annotation { "Feature Type Name" : "Feature", "Feature Type Description" : "" }
export const myFeature = defineFeature(function(context is Context, id is Id, definition is map)
    precondition{}
    {
        {
            var Q0;
            Q0=qCreatedBy(makeId("Front.planeOp"),FACE);
            var sketch = newSketch(context, id + "F0", { "sketchPlane" : qUnion([Q0])});
            skCircle(sketch, "E0", {"center": v(0, 0) * mm, "radius": 10.5 * mm});
            skCircle(sketch, "E1", {"center": v(0, 0) * mm, "radius": 13 * mm});
            skArc(sketch, "E2", {"start": v(11.57, 14.44) * mm, "mid": v(9.32, 12.76) * mm, "end": v(7.8, 10.4) * mm});
            skArc(sketch, "E3.MirrorCS", {"start": v(-11.57, 14.44) * mm, "mid": v(-9.32, 12.76) * mm, "end": v(-7.8, 10.4) * mm});
            skLineSegment(sketch, "E4", {"start": v(11.57, 14.44) * mm, "end": v(-11.57, 14.44) * mm});
            skSolve(sketch);
        }
        {
            var Q0;
            Q0=makeQuery(id+"F0.imprint","IMPRINT",FACE,{"disambiguationData":[TD([[makeQuery(id+"F0.imprint","IMPRINT",EDGE,{"derivedFrom":sQuery(id+"F0.wireOp",EDGE,"E0")}),-1.0]])]});
            extrude(context, id + "F1", {"entities" : qUnion([Q0]), "depth" : 8 * mm, "offsetDistance" : 25 * mm});
        }
        {
            var Q0;
            Q0=makeQuery(id+"F1.opExtrude","CAP_EDGE",EDGE,{"disambiguationData":[OSD([sQuery(id+"F0.wireOp",EDGE,"E1")])],"isStart":true});
            var Q1;
            Q1=makeQuery(id+"F1.opExtrude","CAP_EDGE",EDGE,{"disambiguationData":[OSD([sQuery(id+"F0.wireOp",EDGE,"E1")])],"isStart":false});
            var Q2;
            Q2=makeQuery(id+"F1.opExtrude","CAP_EDGE",EDGE,{"disambiguationData":[OSD([sQuery(id+"F0.wireOp",EDGE,"E0")])],"isStart":false});
            var Q3;
            Q3=makeQuery(id+"F1.opExtrude","CAP_EDGE",EDGE,{"disambiguationData":[OSD([sQuery(id+"F0.wireOp",EDGE,"E0")])],"isStart":true});
            fillet(context, id + "F2", {"entities" : qUnion([Q0, Q1, Q2, Q3]), "radius" : 1 * mm, "tangentPropagation" : true, "allowEdgeOverflow" : false});
        }
        {
            var Q0;
            {var subQ0=sQuery(id+"F0.wireOp",EDGE,"E2");Q0=makeQuery(id+"F0.imprint","IMPRINT",FACE,{"disambiguationData":[TD([[makeQuery(id+"F0.imprint","IMPRINT",EDGE,{"derivedFrom":subQ0}),-1.0]])]});}
            extrude(context, id + "F3", {"entities" : qUnion([Q0]), "operationType" : NewBodyOperationType.ADD, "depth" : 8 * mm, "offsetDistance" : 25 * mm});
        }
        {
            var Q0;
            Q0=makeQuery(id+"F3.opExtrude","SWEPT_FACE",FACE,{"disambiguationData":[OSD([sQuery(id+"F0.wireOp",EDGE,"E4")])]});
            var sketch = newSketch(context, id + "F4", { "sketchPlane" : qUnion([Q0])});
            skCircle(sketch, "E5.cCircle", {"center": v(10.18, -4.7) * mm, "radius": 1 * mm, "construction": true});
            skLineSegment(sketch, "E5.0", {"start": v(9.34, -5.4) * mm, "end": v(9.1, -4.48) * mm});
            skLineSegment(sketch, "E5.1", {"start": v(9.1, -4.48) * mm, "end": v(9.68, -3.72) * mm});
            skLineSegment(sketch, "E5.2", {"start": v(9.68, -3.72) * mm, "end": v(10.64, -3.7) * mm});
            skLineSegment(sketch, "E5.3", {"start": v(10.64, -3.7) * mm, "end": v(11.25, -4.43) * mm});
            skLineSegment(sketch, "E5.4", {"start": v(11.25, -4.43) * mm, "end": v(11.06, -5.37) * mm});
            skLineSegment(sketch, "E5.5", {"start": v(11.06, -5.37) * mm, "end": v(10.2, -5.8) * mm});
            skLineSegment(sketch, "E5.6", {"start": v(10.2, -5.8) * mm, "end": v(9.34, -5.4) * mm});
            skPoint(sketch, "E5.0.midPoint", {"position": v(9.22, -4.94) * mm});
            skCircle(sketch, "E6", {"center": v(10.18, -4.7) * mm, "radius": 1 * mm});
            skText(sketch, "E7", { "text": "Natsu Lee", "fontName": "NotoSansCJKjp-Regular.otf"});
            skLineSegment(sketch, "E8", {"start": v(9.68, -3.72) * mm, "end": v(10.2, -5.8) * mm});
            skLineSegment(sketch, "E9", {"start": v(10.64, -3.7) * mm, "end": v(10.2, -5.8) * mm});
            skCircle(sketch, "E10", {"center": v(-9.7, -1.1) * mm, "radius": 0.75 * mm});
            skArc(sketch, "E11", {"start": v(-9.78, -0.68) * mm, "mid": v(-10, -0.61) * mm, "end": v(-10.16, -0.8) * mm});
            skCircle(sketch, "E12", {"center": v(-9.95, -0.81) * mm, "radius": 0.11 * mm});
            skArc(sketch, "E13", {"start": v(-10.03, -1.41) * mm, "mid": v(-9.63, -1.7) * mm, "end": v(-9.23, -1.41) * mm});
            skArc(sketch, "E14.0", {"start": v(-9.73, -0.64) * mm, "mid": v(-10.03, -0.55) * mm, "end": v(-10.23, -0.8) * mm});
            skLineSegment(sketch, "E15", {"start": v(-10.23, -0.8) * mm, "end": v(-10.16, -0.8) * mm});
            skLineSegment(sketch, "E16", {"start": v(-9.78, -0.68) * mm, "end": v(-9.73, -0.64) * mm});
            skLineSegment(sketch, "E17", {"start": v(-9.63, -0.62) * mm, "end": v(-9.7, -1.1) * mm, "construction": true});
            skCircle(sketch, "E18.MirrorC", {"center": v(-9.38, -0.9) * mm, "radius": 0.11 * mm});
            skArc(sketch, "E19.MirrorCS", {"start": v(-9.5, -0.73) * mm, "mid": v(-9.26, -0.73) * mm, "end": v(-9.18, -0.95) * mm});
            skLineSegment(sketch, "E20.MirrorCS", {"start": v(-9.1, -0.96) * mm, "end": v(-9.18, -0.95) * mm});
            skArc(sketch, "E21.MirrorCS", {"start": v(-9.54, -0.67) * mm, "mid": v(-9.22, -0.67) * mm, "end": v(-9.1, -0.96) * mm});
            skLineSegment(sketch, "E22.MirrorCS", {"start": v(-9.5, -0.73) * mm, "end": v(-9.54, -0.67) * mm});
            skCircle(sketch, "E23", {"center": v(-9.7, -1.1) * mm, "radius": 0.05 * mm});
            skArc(sketch, "E24.0", {"start": v(-10, -1.4) * mm, "mid": v(-9.63, -1.68) * mm, "end": v(-9.25, -1.4) * mm});
            skLineSegment(sketch, "E25", {"start": v(-10.03, -1.41) * mm, "end": v(-10, -1.4) * mm});
            skLineSegment(sketch, "E26", {"start": v(-9.25, -1.4) * mm, "end": v(-9.23, -1.41) * mm});
            skArc(sketch, "E27.1.0.0", {"start": v(-6, -1.4) * mm, "mid": v(-5.63, -1.68) * mm, "end": v(-5.25, -1.4) * mm});
            skArc(sketch, "E27.1.0.1", {"start": v(-6.03, -1.41) * mm, "mid": v(-5.63, -1.7) * mm, "end": v(-5.23, -1.41) * mm});
            skLineSegment(sketch, "E27.1.0.2", {"start": v(-6.03, -1.41) * mm, "end": v(-6, -1.4) * mm});
            skLineSegment(sketch, "E27.1.0.3", {"start": v(-5.25, -1.4) * mm, "end": v(-5.23, -1.41) * mm});
            skCircle(sketch, "E27.1.0.4", {"center": v(-5.7, -1.1) * mm, "radius": 0.05 * mm});
            skCircle(sketch, "E27.1.0.5", {"center": v(-5.95, -0.81) * mm, "radius": 0.11 * mm});
            skArc(sketch, "E27.1.0.6", {"start": v(-5.78, -0.68) * mm, "mid": v(-6, -0.61) * mm, "end": v(-6.16, -0.8) * mm});
            skLineSegment(sketch, "E27.1.0.7", {"start": v(-6.23, -0.8) * mm, "end": v(-6.16, -0.8) * mm});
            skArc(sketch, "E27.1.0.8", {"start": v(-5.73, -0.64) * mm, "mid": v(-6.03, -0.55) * mm, "end": v(-6.23, -0.8) * mm});
            skLineSegment(sketch, "E27.1.0.9", {"start": v(-5.78, -0.68) * mm, "end": v(-5.73, -0.64) * mm});
            skLineSegment(sketch, "E27.1.0.10", {"start": v(-5.5, -0.73) * mm, "end": v(-5.54, -0.67) * mm});
            skArc(sketch, "E27.1.0.11", {"start": v(-5.54, -0.67) * mm, "mid": v(-5.22, -0.67) * mm, "end": v(-5.1, -0.96) * mm});
            skArc(sketch, "E27.1.0.12", {"start": v(-5.5, -0.73) * mm, "mid": v(-5.26, -0.73) * mm, "end": v(-5.18, -0.95) * mm});
            skCircle(sketch, "E27.1.0.13", {"center": v(-5.38, -0.9) * mm, "radius": 0.11 * mm});
            skLineSegment(sketch, "E27.1.0.14", {"start": v(-5.1, -0.96) * mm, "end": v(-5.18, -0.95) * mm});
            skArc(sketch, "E27.2.0.0", {"start": v(-2, -1.4) * mm, "mid": v(-1.63, -1.68) * mm, "end": v(-1.25, -1.4) * mm});
            skArc(sketch, "E27.2.0.1", {"start": v(-2.03, -1.41) * mm, "mid": v(-1.63, -1.7) * mm, "end": v(-1.23, -1.41) * mm});
            skLineSegment(sketch, "E27.2.0.2", {"start": v(-2.03, -1.41) * mm, "end": v(-2, -1.4) * mm});
            skLineSegment(sketch, "E27.2.0.3", {"start": v(-1.25, -1.4) * mm, "end": v(-1.23, -1.41) * mm});
            skCircle(sketch, "E27.2.0.4", {"center": v(-1.7, -1.1) * mm, "radius": 0.05 * mm});
            skCircle(sketch, "E27.2.0.5", {"center": v(-1.95, -0.81) * mm, "radius": 0.11 * mm});
            skArc(sketch, "E27.2.0.6", {"start": v(-1.78, -0.68) * mm, "mid": v(-2, -0.61) * mm, "end": v(-2.16, -0.8) * mm});
            skLineSegment(sketch, "E27.2.0.7", {"start": v(-2.23, -0.8) * mm, "end": v(-2.16, -0.8) * mm});
            skArc(sketch, "E27.2.0.8", {"start": v(-1.73, -0.64) * mm, "mid": v(-2.03, -0.55) * mm, "end": v(-2.23, -0.8) * mm});
            skLineSegment(sketch, "E27.2.0.9", {"start": v(-1.78, -0.68) * mm, "end": v(-1.73, -0.64) * mm});
            skLineSegment(sketch, "E27.2.0.10", {"start": v(-1.5, -0.73) * mm, "end": v(-1.54, -0.67) * mm});
            skArc(sketch, "E27.2.0.11", {"start": v(-1.54, -0.67) * mm, "mid": v(-1.22, -0.67) * mm, "end": v(-1.1, -0.96) * mm});
            skArc(sketch, "E27.2.0.12", {"start": v(-1.5, -0.73) * mm, "mid": v(-1.26, -0.73) * mm, "end": v(-1.18, -0.95) * mm});
            skCircle(sketch, "E27.2.0.13", {"center": v(-1.38, -0.9) * mm, "radius": 0.11 * mm});
            skLineSegment(sketch, "E27.2.0.14", {"start": v(-1.1, -0.96) * mm, "end": v(-1.18, -0.95) * mm});
            skArc(sketch, "E27.3.0.0", {"start": v(2, -1.4) * mm, "mid": v(2.37, -1.68) * mm, "end": v(2.75, -1.4) * mm});
            skArc(sketch, "E27.3.0.1", {"start": v(1.97, -1.41) * mm, "mid": v(2.37, -1.7) * mm, "end": v(2.77, -1.41) * mm});
            skLineSegment(sketch, "E27.3.0.2", {"start": v(1.97, -1.41) * mm, "end": v(2, -1.4) * mm});
            skLineSegment(sketch, "E27.3.0.3", {"start": v(2.75, -1.4) * mm, "end": v(2.77, -1.41) * mm});
            skCircle(sketch, "E27.3.0.4", {"center": v(2.3, -1.1) * mm, "radius": 0.05 * mm});
            skCircle(sketch, "E27.3.0.5", {"center": v(2.05, -0.81) * mm, "radius": 0.11 * mm});
            skArc(sketch, "E27.3.0.6", {"start": v(2.22, -0.68) * mm, "mid": v(2, -0.61) * mm, "end": v(1.84, -0.8) * mm});
            skLineSegment(sketch, "E27.3.0.7", {"start": v(1.77, -0.8) * mm, "end": v(1.84, -0.8) * mm});
            skArc(sketch, "E27.3.0.8", {"start": v(2.27, -0.64) * mm, "mid": v(1.97, -0.55) * mm, "end": v(1.77, -0.8) * mm});
            skLineSegment(sketch, "E27.3.0.9", {"start": v(2.22, -0.68) * mm, "end": v(2.27, -0.64) * mm});
            skLineSegment(sketch, "E27.3.0.10", {"start": v(2.5, -0.73) * mm, "end": v(2.46, -0.67) * mm});
            skArc(sketch, "E27.3.0.11", {"start": v(2.46, -0.67) * mm, "mid": v(2.78, -0.67) * mm, "end": v(2.9, -0.96) * mm});
            skArc(sketch, "E27.3.0.12", {"start": v(2.5, -0.73) * mm, "mid": v(2.74, -0.73) * mm, "end": v(2.82, -0.95) * mm});
            skCircle(sketch, "E27.3.0.13", {"center": v(2.62, -0.9) * mm, "radius": 0.11 * mm});
            skLineSegment(sketch, "E27.3.0.14", {"start": v(2.9, -0.96) * mm, "end": v(2.82, -0.95) * mm});
            skArc(sketch, "E27.4.0.0", {"start": v(6, -1.4) * mm, "mid": v(6.37, -1.68) * mm, "end": v(6.75, -1.4) * mm});
            skArc(sketch, "E27.4.0.1", {"start": v(5.97, -1.41) * mm, "mid": v(6.37, -1.7) * mm, "end": v(6.77, -1.41) * mm});
            skLineSegment(sketch, "E27.4.0.2", {"start": v(5.97, -1.41) * mm, "end": v(6, -1.4) * mm});
            skLineSegment(sketch, "E27.4.0.3", {"start": v(6.75, -1.4) * mm, "end": v(6.77, -1.41) * mm});
            skCircle(sketch, "E27.4.0.4", {"center": v(6.3, -1.1) * mm, "radius": 0.05 * mm});
            skCircle(sketch, "E27.4.0.5", {"center": v(6.05, -0.81) * mm, "radius": 0.11 * mm});
            skArc(sketch, "E27.4.0.6", {"start": v(6.22, -0.68) * mm, "mid": v(6, -0.61) * mm, "end": v(5.84, -0.8) * mm});
            skLineSegment(sketch, "E27.4.0.7", {"start": v(5.77, -0.8) * mm, "end": v(5.84, -0.8) * mm});
            skArc(sketch, "E27.4.0.8", {"start": v(6.27, -0.64) * mm, "mid": v(5.97, -0.55) * mm, "end": v(5.77, -0.8) * mm});
            skLineSegment(sketch, "E27.4.0.9", {"start": v(6.22, -0.68) * mm, "end": v(6.27, -0.64) * mm});
            skLineSegment(sketch, "E27.4.0.10", {"start": v(6.5, -0.73) * mm, "end": v(6.46, -0.67) * mm});
            skArc(sketch, "E27.4.0.11", {"start": v(6.46, -0.67) * mm, "mid": v(6.78, -0.67) * mm, "end": v(6.9, -0.96) * mm});
            skArc(sketch, "E27.4.0.12", {"start": v(6.5, -0.73) * mm, "mid": v(6.74, -0.73) * mm, "end": v(6.82, -0.95) * mm});
            skCircle(sketch, "E27.4.0.13", {"center": v(6.62, -0.9) * mm, "radius": 0.11 * mm});
            skLineSegment(sketch, "E27.4.0.14", {"start": v(6.9, -0.96) * mm, "end": v(6.82, -0.95) * mm});
            skArc(sketch, "E27.5.0.0", {"start": v(10, -1.4) * mm, "mid": v(10.37, -1.68) * mm, "end": v(10.75, -1.4) * mm});
            skArc(sketch, "E27.5.0.1", {"start": v(9.97, -1.41) * mm, "mid": v(10.37, -1.7) * mm, "end": v(10.77, -1.41) * mm});
            skLineSegment(sketch, "E27.5.0.2", {"start": v(9.97, -1.41) * mm, "end": v(10, -1.4) * mm});
            skLineSegment(sketch, "E27.5.0.3", {"start": v(10.75, -1.4) * mm, "end": v(10.77, -1.41) * mm});
            skCircle(sketch, "E27.5.0.4", {"center": v(10.3, -1.1) * mm, "radius": 0.05 * mm});
            skCircle(sketch, "E27.5.0.5", {"center": v(10.05, -0.81) * mm, "radius": 0.11 * mm});
            skArc(sketch, "E27.5.0.6", {"start": v(10.22, -0.68) * mm, "mid": v(10, -0.61) * mm, "end": v(9.84, -0.8) * mm});
            skLineSegment(sketch, "E27.5.0.7", {"start": v(9.77, -0.8) * mm, "end": v(9.84, -0.8) * mm});
            skArc(sketch, "E27.5.0.8", {"start": v(10.27, -0.64) * mm, "mid": v(9.97, -0.55) * mm, "end": v(9.77, -0.8) * mm});
            skLineSegment(sketch, "E27.5.0.9", {"start": v(10.22, -0.68) * mm, "end": v(10.27, -0.64) * mm});
            skLineSegment(sketch, "E27.5.0.10", {"start": v(10.5, -0.73) * mm, "end": v(10.46, -0.67) * mm});
            skArc(sketch, "E27.5.0.11", {"start": v(10.46, -0.67) * mm, "mid": v(10.78, -0.67) * mm, "end": v(10.9, -0.96) * mm});
            skArc(sketch, "E27.5.0.12", {"start": v(10.5, -0.73) * mm, "mid": v(10.74, -0.73) * mm, "end": v(10.82, -0.95) * mm});
            skCircle(sketch, "E27.5.0.13", {"center": v(10.62, -0.9) * mm, "radius": 0.11 * mm});
            skLineSegment(sketch, "E27.5.0.14", {"start": v(10.9, -0.96) * mm, "end": v(10.82, -0.95) * mm});
            skLineSegment(sketch, "E27.direction1", {"start": v(-10, -1.4) * mm, "end": v(-6, -1.4) * mm, "construction": true});
            const initialGuessF4  = {"E7": [-0.01103, -0.00537, 1, 0, 0.00311]};
            skSetInitialGuess(sketch, initialGuessF4);
            skSolve(sketch);
        }
        {
            var Q0;
            {var subQ0=sQuery(id+"F4.wireOp",EDGE,"E5.5");var subQ1=sQuery(id+"F4.wireOp",EDGE,"E5.4");var subQ2=makeQuery(id+"F4.imprint","INTERSECT",VERTEX,{"derivedFrom":[subQ1,subQ0]});Q0=makeQuery(id+"F4.imprint","IMPRINT",FACE,{"disambiguationData":[TD([[makeQuery(id+"F4.imprint","IMPRINT",EDGE,{"disambiguationData":[TD([[subQ2,1.0]])],"derivedFrom":subQ1}),-1.0]])]});}
            var Q1;
            {var subQ0=sQuery(id+"F4.wireOp",EDGE,"E5.4");var subQ1=sQuery(id+"F4.wireOp",EDGE,"E5.3");var subQ2=makeQuery(id+"F4.imprint","INTERSECT",VERTEX,{"derivedFrom":[subQ1,subQ0]});Q1=makeQuery(id+"F4.imprint","IMPRINT",FACE,{"disambiguationData":[TD([[makeQuery(id+"F4.imprint","IMPRINT",EDGE,{"disambiguationData":[TD([[subQ2,1.0]])],"derivedFrom":subQ1}),-1.0]])]});}
            var Q2;
            {var subQ0=sQuery(id+"F4.wireOp",EDGE,"E5.3");var subQ1=sQuery(id+"F4.wireOp",EDGE,"E5.2");var subQ2=makeQuery(id+"F4.imprint","INTERSECT",VERTEX,{"derivedFrom":[subQ1,subQ0]});Q2=makeQuery(id+"F4.imprint","IMPRINT",FACE,{"disambiguationData":[TD([[makeQuery(id+"F4.imprint","IMPRINT",EDGE,{"disambiguationData":[TD([[subQ2,1.0]])],"derivedFrom":subQ1}),-1.0]])]});}
            var Q3;
            {var subQ0=sQuery(id+"F4.wireOp",EDGE,"E5.2");var subQ1=sQuery(id+"F4.wireOp",EDGE,"E5.1");var subQ2=makeQuery(id+"F4.imprint","INTERSECT",VERTEX,{"derivedFrom":[subQ1,subQ0]});Q3=makeQuery(id+"F4.imprint","IMPRINT",FACE,{"disambiguationData":[TD([[makeQuery(id+"F4.imprint","IMPRINT",EDGE,{"disambiguationData":[TD([[subQ2,1.0]])],"derivedFrom":subQ1}),-1.0]])]});}
            var Q4;
            {var subQ0=sQuery(id+"F4.wireOp",EDGE,"E5.1");var subQ1=sQuery(id+"F4.wireOp",EDGE,"E5.0");var subQ2=makeQuery(id+"F4.imprint","INTERSECT",VERTEX,{"derivedFrom":[subQ1,subQ0]});Q4=makeQuery(id+"F4.imprint","IMPRINT",FACE,{"disambiguationData":[TD([[makeQuery(id+"F4.imprint","IMPRINT",EDGE,{"disambiguationData":[TD([[subQ2,1.0]])],"derivedFrom":subQ1}),-1.0]])]});}
            var Q5;
            {var subQ0=sQuery(id+"F4.wireOp",EDGE,"E5.6");var subQ1=sQuery(id+"F4.wireOp",EDGE,"E5.0");var subQ2=makeQuery(id+"F4.imprint","INTERSECT",VERTEX,{"derivedFrom":[subQ1,subQ0]});Q5=makeQuery(id+"F4.imprint","IMPRINT",FACE,{"disambiguationData":[TD([[makeQuery(id+"F4.imprint","IMPRINT",EDGE,{"disambiguationData":[TD([[subQ2,-1.0]])],"derivedFrom":subQ1}),-1.0]])]});}
            var Q6;
            {var subQ0=sQuery(id+"F4.wireOp",EDGE,"E5.6");var subQ1=sQuery(id+"F4.wireOp",EDGE,"E5.5");var subQ2=makeQuery(id+"F4.imprint","INTERSECT",VERTEX,{"derivedFrom":[subQ1,subQ0]});Q6=makeQuery(id+"F4.imprint","IMPRINT",FACE,{"disambiguationData":[TD([[makeQuery(id+"F4.imprint","IMPRINT",EDGE,{"disambiguationData":[TD([[subQ2,1.0]])],"derivedFrom":subQ1}),-1.0]])]});}
            extrude(context, id + "F5", {"entities" : qUnion([Q0, Q1, Q2, Q3, Q4, Q5, Q6]), "operationType" : NewBodyOperationType.ADD, "depth" : 1 * mm, "offsetDistance" : 25 * mm});
        }
        {
            var Q0;
            Q0=makeQuery(id+"F4.imprint","IMPRINT",FACE,{"disambiguationData":[TD([[makeQuery(id+"F4.imprint","IMPRINT",EDGE,{"derivedFrom":sQuery(id+"F4.wireOp",EDGE,"E7.sketch_text.stroke-0")}),1.0]])]});
            var Q1;
            Q1=makeQuery(id+"F4.imprint","IMPRINT",FACE,{"disambiguationData":[TD([[makeQuery(id+"F4.imprint","IMPRINT",EDGE,{"derivedFrom":sQuery(id+"F4.wireOp",EDGE,"E7.sketch_text.stroke-16")}),1.0]])]});
            var Q2;
            Q2=makeQuery(id+"F4.imprint","IMPRINT",FACE,{"disambiguationData":[TD([[makeQuery(id+"F4.imprint","IMPRINT",EDGE,{"derivedFrom":sQuery(id+"F4.wireOp",EDGE,"E7.sketch_text.stroke-32")}),1.0]])]});
            var Q3;
            Q3=makeQuery(id+"F4.imprint","IMPRINT",FACE,{"disambiguationData":[TD([[makeQuery(id+"F4.imprint","IMPRINT",EDGE,{"derivedFrom":sQuery(id+"F4.wireOp",EDGE,"E7.sketch_text.stroke-48")}),1.0]])]});
            var Q4;
            Q4=makeQuery(id+"F4.imprint","IMPRINT",FACE,{"disambiguationData":[TD([[makeQuery(id+"F4.imprint","IMPRINT",EDGE,{"derivedFrom":sQuery(id+"F4.wireOp",EDGE,"E7.sketch_text.stroke-62")}),1.0]])]});
            var Q5;
            Q5=makeQuery(id+"F4.imprint","IMPRINT",FACE,{"disambiguationData":[TD([[makeQuery(id+"F4.imprint","IMPRINT",EDGE,{"derivedFrom":sQuery(id+"F4.wireOp",EDGE,"E7.sketch_text.stroke-75")}),1.0]])]});
            var Q6;
            Q6=makeQuery(id+"F4.imprint","IMPRINT",FACE,{"disambiguationData":[TD([[makeQuery(id+"F4.imprint","IMPRINT",EDGE,{"derivedFrom":sQuery(id+"F4.wireOp",EDGE,"E7.sketch_text.stroke-81")}),1.0]])]});
            var Q7;
            Q7=makeQuery(id+"F4.imprint","IMPRINT",FACE,{"disambiguationData":[TD([[makeQuery(id+"F4.imprint","IMPRINT",EDGE,{"derivedFrom":sQuery(id+"F4.wireOp",EDGE,"E7.sketch_text.stroke-93")}),1.0]])]});
            extrude(context, id + "F6", {"entities" : qUnion([Q0, Q1, Q2, Q3, Q4, Q5, Q6, Q7]), "operationType" : NewBodyOperationType.ADD, "depth" : .5 * mm, "offsetDistance" : 25 * mm});
        }
        {
            var Q0;
            Q0=makeQuery(id+"F4.imprint","IMPRINT",FACE,{"disambiguationData":[TD([[makeQuery(id+"F4.imprint","IMPRINT",EDGE,{"derivedFrom":sQuery(id+"F4.wireOp",EDGE,"E11")}),-1.0]])]});
            var Q1;
            Q1=makeQuery(id+"F4.imprint","IMPRINT",FACE,{"disambiguationData":[TD([[makeQuery(id+"F4.imprint","IMPRINT",EDGE,{"derivedFrom":sQuery(id+"F4.wireOp",EDGE,"E12")}),1.0]])]});
            var Q2;
            Q2=makeQuery(id+"F4.imprint","IMPRINT",FACE,{"disambiguationData":[TD([[makeQuery(id+"F4.imprint","IMPRINT",EDGE,{"derivedFrom":sQuery(id+"F4.wireOp",EDGE,"E19.MirrorCS")}),1.0]])]});
            var Q3;
            Q3=makeQuery(id+"F4.imprint","IMPRINT",FACE,{"disambiguationData":[TD([[makeQuery(id+"F4.imprint","IMPRINT",EDGE,{"derivedFrom":sQuery(id+"F4.wireOp",EDGE,"E18.MirrorC")}),-1.0]])]});
            var Q4;
            Q4=makeQuery(id+"F4.imprint","IMPRINT",FACE,{"disambiguationData":[TD([[makeQuery(id+"F4.imprint","IMPRINT",EDGE,{"derivedFrom":sQuery(id+"F4.wireOp",EDGE,"E13")}),1.0]])]});
            var Q5;
            Q5=makeQuery(id+"F4.imprint","IMPRINT",FACE,{"disambiguationData":[TD([[makeQuery(id+"F4.imprint","IMPRINT",EDGE,{"derivedFrom":sQuery(id+"F4.wireOp",EDGE,"E23")}),1.0]])]});
            extrude(context, id + "F7", {"entities" : qUnion([Q0, Q1, Q2, Q3, Q4, Q5]), "operationType" : NewBodyOperationType.ADD, "depth" : .5 * mm, "offsetDistance" : 25 * mm});
        }
        {
            var Q0;
            Q0=makeQuery(id+"F4.imprint","IMPRINT",FACE,{"disambiguationData":[TD([[makeQuery(id+"F4.imprint","IMPRINT",EDGE,{"derivedFrom":sQuery(id+"F4.wireOp",EDGE,"E27.1.0.0")}),-1.0]])]});
            var Q1;
            Q1=makeQuery(id+"F4.imprint","IMPRINT",FACE,{"disambiguationData":[TD([[makeQuery(id+"F4.imprint","IMPRINT",EDGE,{"derivedFrom":sQuery(id+"F4.wireOp",EDGE,"E27.1.0.6")}),-1.0]])]});
            var Q2;
            Q2=makeQuery(id+"F4.imprint","IMPRINT",FACE,{"disambiguationData":[TD([[makeQuery(id+"F4.imprint","IMPRINT",EDGE,{"derivedFrom":sQuery(id+"F4.wireOp",EDGE,"E27.1.0.5")}),1.0]])]});
            var Q3;
            Q3=makeQuery(id+"F4.imprint","IMPRINT",FACE,{"disambiguationData":[TD([[makeQuery(id+"F4.imprint","IMPRINT",EDGE,{"derivedFrom":sQuery(id+"F4.wireOp",EDGE,"E27.1.0.13")}),-1.0]])]});
            var Q4;
            Q4=makeQuery(id+"F4.imprint","IMPRINT",FACE,{"disambiguationData":[TD([[makeQuery(id+"F4.imprint","IMPRINT",EDGE,{"derivedFrom":sQuery(id+"F4.wireOp",EDGE,"E27.1.0.4")}),1.0]])]});
            var Q5;
            Q5=makeQuery(id+"F4.imprint","IMPRINT",FACE,{"disambiguationData":[TD([[makeQuery(id+"F4.imprint","IMPRINT",EDGE,{"derivedFrom":sQuery(id+"F4.wireOp",EDGE,"E27.1.0.10")}),-1.0]])]});
            var Q6;
            Q6=makeQuery(id+"F4.imprint","IMPRINT",FACE,{"disambiguationData":[TD([[makeQuery(id+"F4.imprint","IMPRINT",EDGE,{"derivedFrom":sQuery(id+"F4.wireOp",EDGE,"E27.2.0.5")}),1.0]])]});
            var Q7;
            Q7=makeQuery(id+"F4.imprint","IMPRINT",FACE,{"disambiguationData":[TD([[makeQuery(id+"F4.imprint","IMPRINT",EDGE,{"derivedFrom":sQuery(id+"F4.wireOp",EDGE,"E27.2.0.6")}),-1.0]])]});
            var Q8;
            Q8=makeQuery(id+"F4.imprint","IMPRINT",FACE,{"disambiguationData":[TD([[makeQuery(id+"F4.imprint","IMPRINT",EDGE,{"derivedFrom":sQuery(id+"F4.wireOp",EDGE,"E27.2.0.0")}),-1.0]])]});
            var Q9;
            Q9=makeQuery(id+"F4.imprint","IMPRINT",FACE,{"disambiguationData":[TD([[makeQuery(id+"F4.imprint","IMPRINT",EDGE,{"derivedFrom":sQuery(id+"F4.wireOp",EDGE,"E27.2.0.4")}),1.0]])]});
            var Q10;
            Q10=makeQuery(id+"F4.imprint","IMPRINT",FACE,{"disambiguationData":[TD([[makeQuery(id+"F4.imprint","IMPRINT",EDGE,{"derivedFrom":sQuery(id+"F4.wireOp",EDGE,"E27.2.0.13")}),-1.0]])]});
            var Q11;
            Q11=makeQuery(id+"F4.imprint","IMPRINT",FACE,{"disambiguationData":[TD([[makeQuery(id+"F4.imprint","IMPRINT",EDGE,{"derivedFrom":sQuery(id+"F4.wireOp",EDGE,"E27.2.0.10")}),-1.0]])]});
            var Q12;
            Q12=makeQuery(id+"F4.imprint","IMPRINT",FACE,{"disambiguationData":[TD([[makeQuery(id+"F4.imprint","IMPRINT",EDGE,{"derivedFrom":sQuery(id+"F4.wireOp",EDGE,"E27.3.0.6")}),-1.0]])]});
            var Q13;
            Q13=makeQuery(id+"F4.imprint","IMPRINT",FACE,{"disambiguationData":[TD([[makeQuery(id+"F4.imprint","IMPRINT",EDGE,{"derivedFrom":sQuery(id+"F4.wireOp",EDGE,"E27.3.0.5")}),1.0]])]});
            var Q14;
            Q14=makeQuery(id+"F4.imprint","IMPRINT",FACE,{"disambiguationData":[TD([[makeQuery(id+"F4.imprint","IMPRINT",EDGE,{"derivedFrom":sQuery(id+"F4.wireOp",EDGE,"E27.3.0.4")}),1.0]])]});
            var Q15;
            Q15=makeQuery(id+"F4.imprint","IMPRINT",FACE,{"disambiguationData":[TD([[makeQuery(id+"F4.imprint","IMPRINT",EDGE,{"derivedFrom":sQuery(id+"F4.wireOp",EDGE,"E27.3.0.0")}),-1.0]])]});
            var Q16;
            Q16=makeQuery(id+"F4.imprint","IMPRINT",FACE,{"disambiguationData":[TD([[makeQuery(id+"F4.imprint","IMPRINT",EDGE,{"derivedFrom":sQuery(id+"F4.wireOp",EDGE,"E27.3.0.13")}),-1.0]])]});
            var Q17;
            Q17=makeQuery(id+"F4.imprint","IMPRINT",FACE,{"disambiguationData":[TD([[makeQuery(id+"F4.imprint","IMPRINT",EDGE,{"derivedFrom":sQuery(id+"F4.wireOp",EDGE,"E27.3.0.10")}),-1.0]])]});
            var Q18;
            Q18=makeQuery(id+"F4.imprint","IMPRINT",FACE,{"disambiguationData":[TD([[makeQuery(id+"F4.imprint","IMPRINT",EDGE,{"derivedFrom":sQuery(id+"F4.wireOp",EDGE,"E27.4.0.6")}),-1.0]])]});
            var Q19;
            Q19=makeQuery(id+"F4.imprint","IMPRINT",FACE,{"disambiguationData":[TD([[makeQuery(id+"F4.imprint","IMPRINT",EDGE,{"derivedFrom":sQuery(id+"F4.wireOp",EDGE,"E27.4.0.5")}),1.0]])]});
            var Q20;
            Q20=makeQuery(id+"F4.imprint","IMPRINT",FACE,{"disambiguationData":[TD([[makeQuery(id+"F4.imprint","IMPRINT",EDGE,{"derivedFrom":sQuery(id+"F4.wireOp",EDGE,"E27.4.0.0")}),-1.0]])]});
            var Q21;
            Q21=makeQuery(id+"F4.imprint","IMPRINT",FACE,{"disambiguationData":[TD([[makeQuery(id+"F4.imprint","IMPRINT",EDGE,{"derivedFrom":sQuery(id+"F4.wireOp",EDGE,"E27.4.0.4")}),1.0]])]});
            var Q22;
            Q22=makeQuery(id+"F4.imprint","IMPRINT",FACE,{"disambiguationData":[TD([[makeQuery(id+"F4.imprint","IMPRINT",EDGE,{"derivedFrom":sQuery(id+"F4.wireOp",EDGE,"E27.4.0.13")}),-1.0]])]});
            var Q23;
            Q23=makeQuery(id+"F4.imprint","IMPRINT",FACE,{"disambiguationData":[TD([[makeQuery(id+"F4.imprint","IMPRINT",EDGE,{"derivedFrom":sQuery(id+"F4.wireOp",EDGE,"E27.4.0.10")}),-1.0]])]});
            var Q24;
            Q24=makeQuery(id+"F4.imprint","IMPRINT",FACE,{"disambiguationData":[TD([[makeQuery(id+"F4.imprint","IMPRINT",EDGE,{"derivedFrom":sQuery(id+"F4.wireOp",EDGE,"E27.5.0.6")}),-1.0]])]});
            var Q25;
            Q25=makeQuery(id+"F4.imprint","IMPRINT",FACE,{"disambiguationData":[TD([[makeQuery(id+"F4.imprint","IMPRINT",EDGE,{"derivedFrom":sQuery(id+"F4.wireOp",EDGE,"E27.5.0.5")}),1.0]])]});
            var Q26;
            Q26=makeQuery(id+"F4.imprint","IMPRINT",FACE,{"disambiguationData":[TD([[makeQuery(id+"F4.imprint","IMPRINT",EDGE,{"derivedFrom":sQuery(id+"F4.wireOp",EDGE,"E27.5.0.4")}),1.0]])]});
            var Q27;
            Q27=makeQuery(id+"F4.imprint","IMPRINT",FACE,{"disambiguationData":[TD([[makeQuery(id+"F4.imprint","IMPRINT",EDGE,{"derivedFrom":sQuery(id+"F4.wireOp",EDGE,"E27.5.0.10")}),-1.0]])]});
            var Q28;
            Q28=makeQuery(id+"F4.imprint","IMPRINT",FACE,{"disambiguationData":[TD([[makeQuery(id+"F4.imprint","IMPRINT",EDGE,{"derivedFrom":sQuery(id+"F4.wireOp",EDGE,"E27.5.0.0")}),-1.0]])]});
            var Q29;
            Q29=makeQuery(id+"F4.imprint","IMPRINT",FACE,{"disambiguationData":[TD([[makeQuery(id+"F4.imprint","IMPRINT",EDGE,{"derivedFrom":sQuery(id+"F4.wireOp",EDGE,"E27.5.0.13")}),-1.0]])]});
            extrude(context, id + "F8", {"entities" : qUnion([Q0, Q1, Q2, Q3, Q4, Q5, Q6, Q7, Q8, Q9, Q10, Q11, Q12, Q13, Q14, Q15, Q16, Q17, Q18, Q19, Q20, Q21, Q22, Q23, Q24, Q25, Q26, Q27, Q28, Q29]), "operationType" : NewBodyOperationType.ADD, "depth" : .5 * mm, "offsetDistance" : 25 * mm});
        }
    });